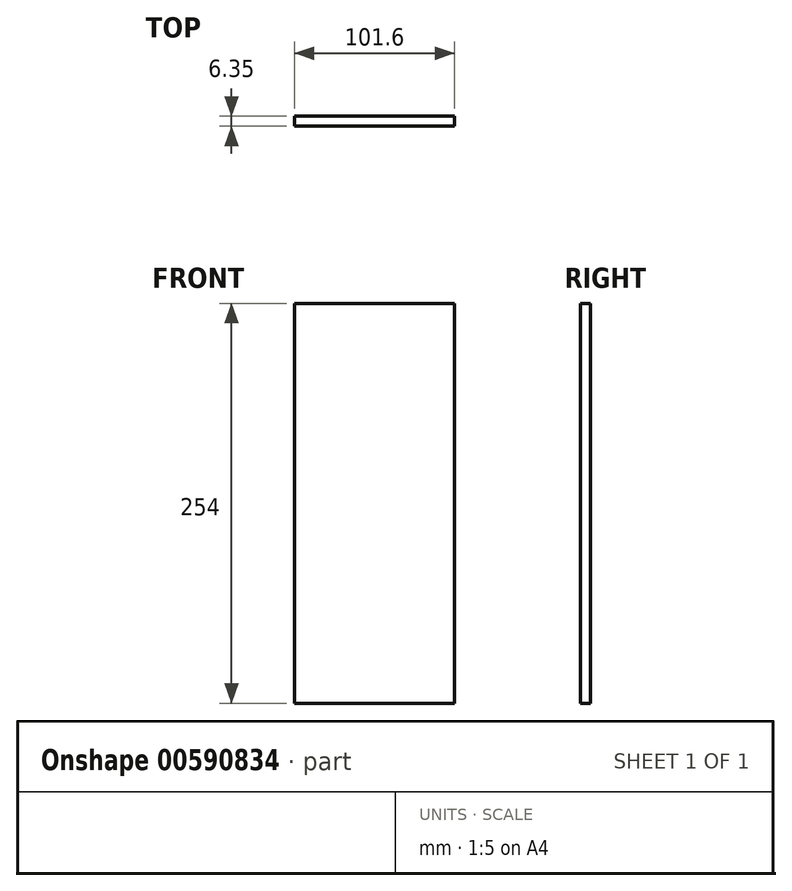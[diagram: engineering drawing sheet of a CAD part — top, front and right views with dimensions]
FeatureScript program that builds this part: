
annotation { "Feature Type Name" : "Feature", "Feature Type Description" : "" }
export const myFeature = defineFeature(function(context is Context, id is Id, definition is map)
    precondition{}
    {
        {
            var Q0;
            Q0=qCreatedBy(makeId("Front.planeOp"),FACE);
            var sketch = newSketch(context, id + "F0", { "sketchPlane" : qUnion([Q0])});
            skLineSegment(sketch, "E0", {"start": v(-61.16, 221.75) * mm, "end": v(40.44, 221.75) * mm});
            skLineSegment(sketch, "E1", {"start": v(40.44, 221.75) * mm, "end": v(40.44, -32.25) * mm});
            skLineSegment(sketch, "E2", {"start": v(40.44, -32.25) * mm, "end": v(-61.16, -32.25) * mm});
            skLineSegment(sketch, "E3", {"start": v(-61.16, -32.25) * mm, "end": v(-61.16, 221.75) * mm});
            skSolve(sketch);
        }
        {
            var Q0;
            Q0=makeQuery(id+"F0.imprint","IMPRINT",FACE,{"disambiguationData":[TD([[makeQuery(id+"F0.imprint","IMPRINT",EDGE,{"derivedFrom":sQuery(id+"F0.wireOp",EDGE,"E0")}),-1.0]])]});
            extrude(context, id + "F1", {"entities" : qUnion([Q0]), "depth" : 6.35 * mm, "offsetDistance" : 25.4 * mm});
        }
    });
